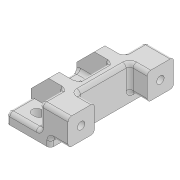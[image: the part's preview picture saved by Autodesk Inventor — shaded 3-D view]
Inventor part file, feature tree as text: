
AUTODESK INVENTOR PART (.ipt)
format: ipt  version: 2020 (Build 240168000, 168)  size: 331,776 bytes
history: native  units: mm
features: extrude x8, sketch x8, chamfer x2, other x1, fillet x1
ambient origin geometry x8: Origin, YZ Plane, XZ Plane, XY Plane, X Axis, Y Axis, Z Axis, Center Point
bodies: Body1 (feature_tree)
feature tree (20):
  other  "Sólido1"
  extrude  "Extrusão1"  Depth=20.0mm
  extrude  "Extrusão2"  Depth=6.0mm
  extrude  "Extrusão3"  Depth=6.0mm TaperAngle=0.0deg
  extrude  "Extrusão4"  TaperAngle=0.0deg  [1 undecoded]
  extrude  "Extrusão5"  Depth=15.0mm
  extrude  "Extrusão6"  Depth=4.2mm
  extrude  "Extrusão7"  Depth=10.0mm TaperAngle=0.0deg
  chamfer  "Chanfro3"  Distance=7.5mm
  fillet  "Arredondamento1"  Radius=7.5mm
  extrude  "Extrusão8"  Depth=2.0mm
  chamfer  "Chanfro4"  Distance=50.0mm
  sketch  "Esboço1"  dims[d0=25.0mm d1=20.0mm]
  sketch  "Esboço2"  dims[d2=60.0mm d3=0.0mm d4=6.0mm]
  sketch  "Esboço3"  dims[d5=6.0mm d6=40.0mm d7=0.0mm]
  sketch  "Esboço4"  dims[d8=15.0mm d9=0.0mm]
  sketch  "Esboço5"  dims[d10=0.0mm d11=15.0mm]
  sketch  "Esboço6"  dims[d12=15.0mm d13=4.2mm]
  sketch  "Esboço7"  dims[d14=4.2mm d15=10.0mm d16=0.0mm]
  sketch  "Esboço8"  dims[d17=7.5mm d18=7.5mm d19=7.5mm d20=7.5mm d21=50.0mm d22=0.0mm d23=6.9mm d24=6.9mm d25=6.0mm d26=0.0mm d27=5.3mm d28=5.3mm d29=8.0mm d30=8.0mm d31=10.0mm d32=0.0mm d33=6.0mm d34=6.0mm d35=14.0mm d36=14.0mm d37=19.0mm d38=0.0mm d45=33.0mm d46=18.0mm d47=45.0deg d48=2.0mm d49=1.5mm d50=1.5mm d51=19.0mm d52=0.0mm d53=10.0mm d54=2.0mm d55=45.0deg d56=0.0mm]
note: 1 required parameter value undecoded (feature->parameter linkage not recoverable at this tier; creation-order binding heuristic only, values carry confidence <= 0.55)
